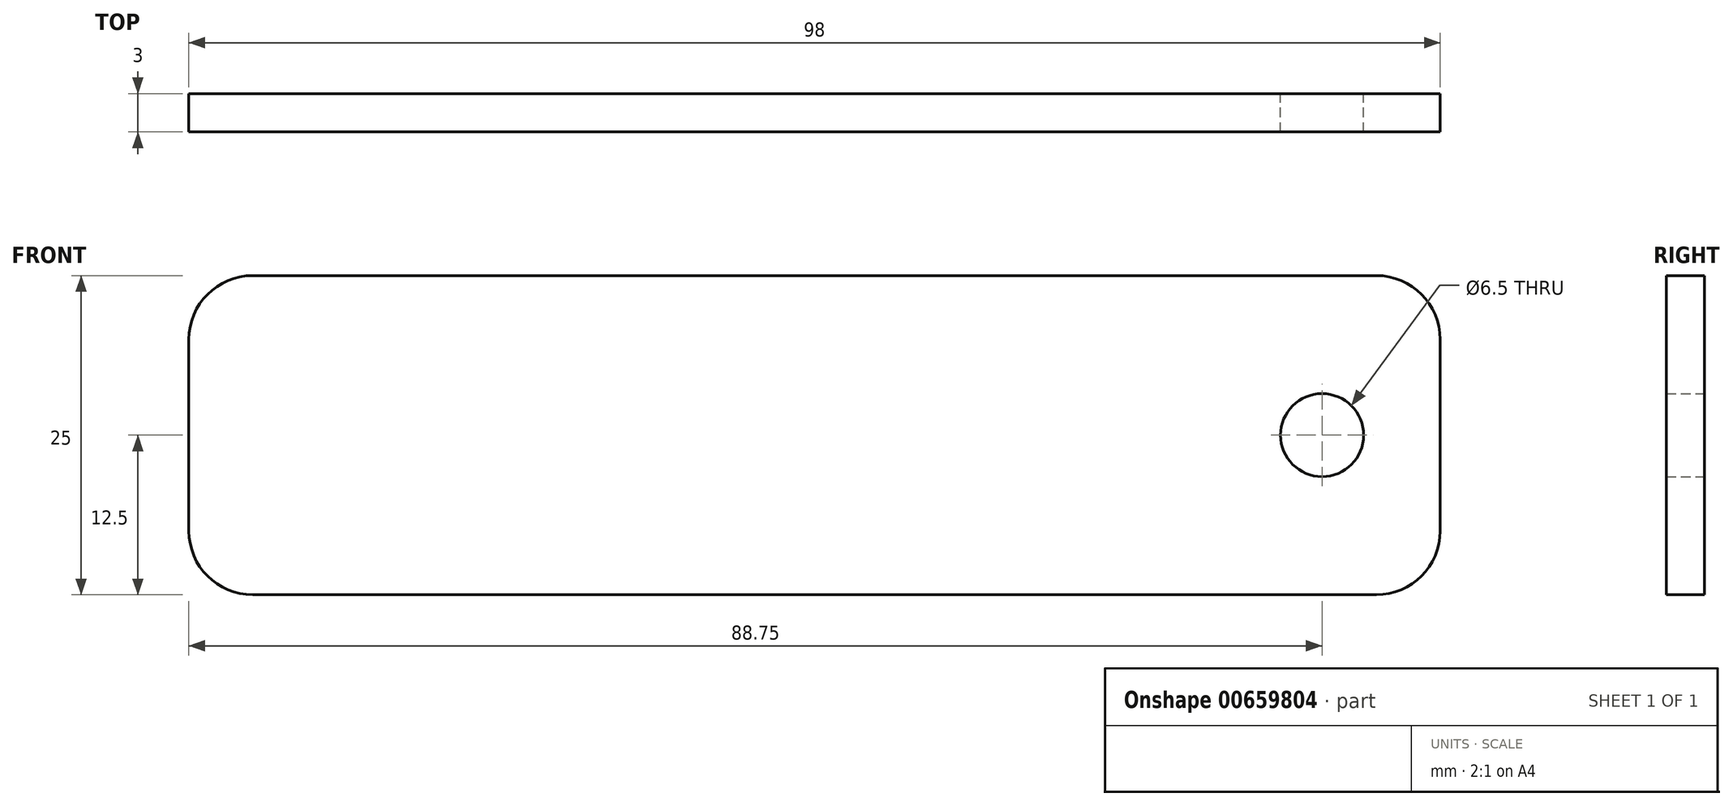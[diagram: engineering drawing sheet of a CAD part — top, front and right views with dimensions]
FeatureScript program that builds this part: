
annotation { "Feature Type Name" : "Feature", "Feature Type Description" : "" }
export const myFeature = defineFeature(function(context is Context, id is Id, definition is map)
    precondition{}
    {
        {
            var Q0;
            Q0=qCreatedBy(makeId("Front.planeOp"),FACE);
            var sketch = newSketch(context, id + "F0", { "sketchPlane" : qUnion([Q0])});
            skLineSegment(sketch, "E0.bottom", {"start": v(44, -12.5) * mm, "end": v(-44, -12.5) * mm});
            skLineSegment(sketch, "E0.top", {"start": v(44, 12.5) * mm, "end": v(-44, 12.5) * mm});
            skLineSegment(sketch, "E0.left", {"start": v(49, -7.5) * mm, "end": v(49, 7.5) * mm});
            skLineSegment(sketch, "E0.right", {"start": v(-49, -7.5) * mm, "end": v(-49, 7.5) * mm});
            skPoint(sketch, "E0.middle", {"position": v(0, 0) * mm});
            skCircle(sketch, "E1", {"center": v(39.75, 0) * mm, "radius": 3.25 * mm});
            skPoint(sketch, "E2.visualSharp", {"position": v(49, 12.5) * mm});
            skArc(sketch, "E2.filletArc", {"start": v(49, 7.5) * mm, "mid": v(47.54, 11.04) * mm, "end": v(44, 12.5) * mm});
            skPoint(sketch, "E3.visualSharp", {"position": v(49, -12.5) * mm});
            skArc(sketch, "E3.filletArc", {"start": v(44, -12.5) * mm, "mid": v(47.54, -11.04) * mm, "end": v(49, -7.5) * mm});
            skPoint(sketch, "E4.visualSharp", {"position": v(-49, -12.5) * mm});
            skArc(sketch, "E4.filletArc", {"start": v(-49, -7.5) * mm, "mid": v(-47.54, -11.04) * mm, "end": v(-44, -12.5) * mm});
            skPoint(sketch, "E5.visualSharp", {"position": v(-49, 12.5) * mm});
            skArc(sketch, "E5.filletArc", {"start": v(-44, 12.5) * mm, "mid": v(-47.54, 11.04) * mm, "end": v(-49, 7.5) * mm});
            skSolve(sketch);
        }
        {
            var Q0;
            Q0=makeQuery(id+"F0.imprint","IMPRINT",FACE,{"disambiguationData":[TD([[makeQuery(id+"F0.imprint","IMPRINT",EDGE,{"derivedFrom":sQuery(id+"F0.wireOp",EDGE,"E0.bottom")}),-1.0]])]});
            extrude(context, id + "F1", {"entities" : qUnion([Q0]), "depth" : 3 * mm, "offsetDistance" : 25 * mm});
        }
    });
